# Revit family: Accessory-Drawer_Pull-KOHLER-HARKEN -K-33561_1
name_source: partatom
category: Specialty Equipment
revit_build: Autodesk Revit 2017 (Build: 20160225_1515(x64)
units: mm (PartAtom-declared; Revit-internal decimal feet)

## family parameters
Cut with Voids When Loaded = No
Host = Face
OmniClass Number = 23.31.25.00
OmniClass Title = Toilet and Bath Specialties
Part Type = Normal
Room Calculation Point = No
Round Connector Dimension = Use Diameter
Shared = No

## types (4) — shared parameters
ADA Compliant = No
Assembly Code = C1030200
Date Modified = 02/19/2021
Default Elevation = 42"
Description = DRAWER PULL 13 INCHES
Height = 1 3/8"
Length = 1 13/16"
Manufacturer = KOHLER Co.
Master Format 2014 = 10 28 00
Master Format 2014 Name = Toilet, Bath, and Laundry Accessories
Material = Premium Metal Construction
Product Documentation Link = https://www.us.kohler.com
Product Name = HARKEN
Product Page URL = http://www.us.kohler.com
URL = https://www.us.kohler.com
WaterSense Certified = No
Width = 12 13/16"

## per-type parameters (varying)
| type | Finish | Model | Type |
| CP-Polished Chrome | Kohler-Metal-CP-Polished_Chrome | K-33561-CP | 1 |
| BN-Vibrant Brushed Nickel | Kohler-Metal-BN-Vibrant_Brushed_Nickel | K-33561-BN | 2 |
| BL-Matte Black | Kohler-Metal-BL-Matte_Black | K-33561-BL | 3 |
| 2MB-Vibrant Brushed Moderne Brass | Kohler-Metal-2MB-Vibrant_Brushed_Moderne_Brass | K-33561-2MB | 4 |

## geometry (parser evidence)
native form markers: Sweep x3
no freeform markers — native parametric forms only
